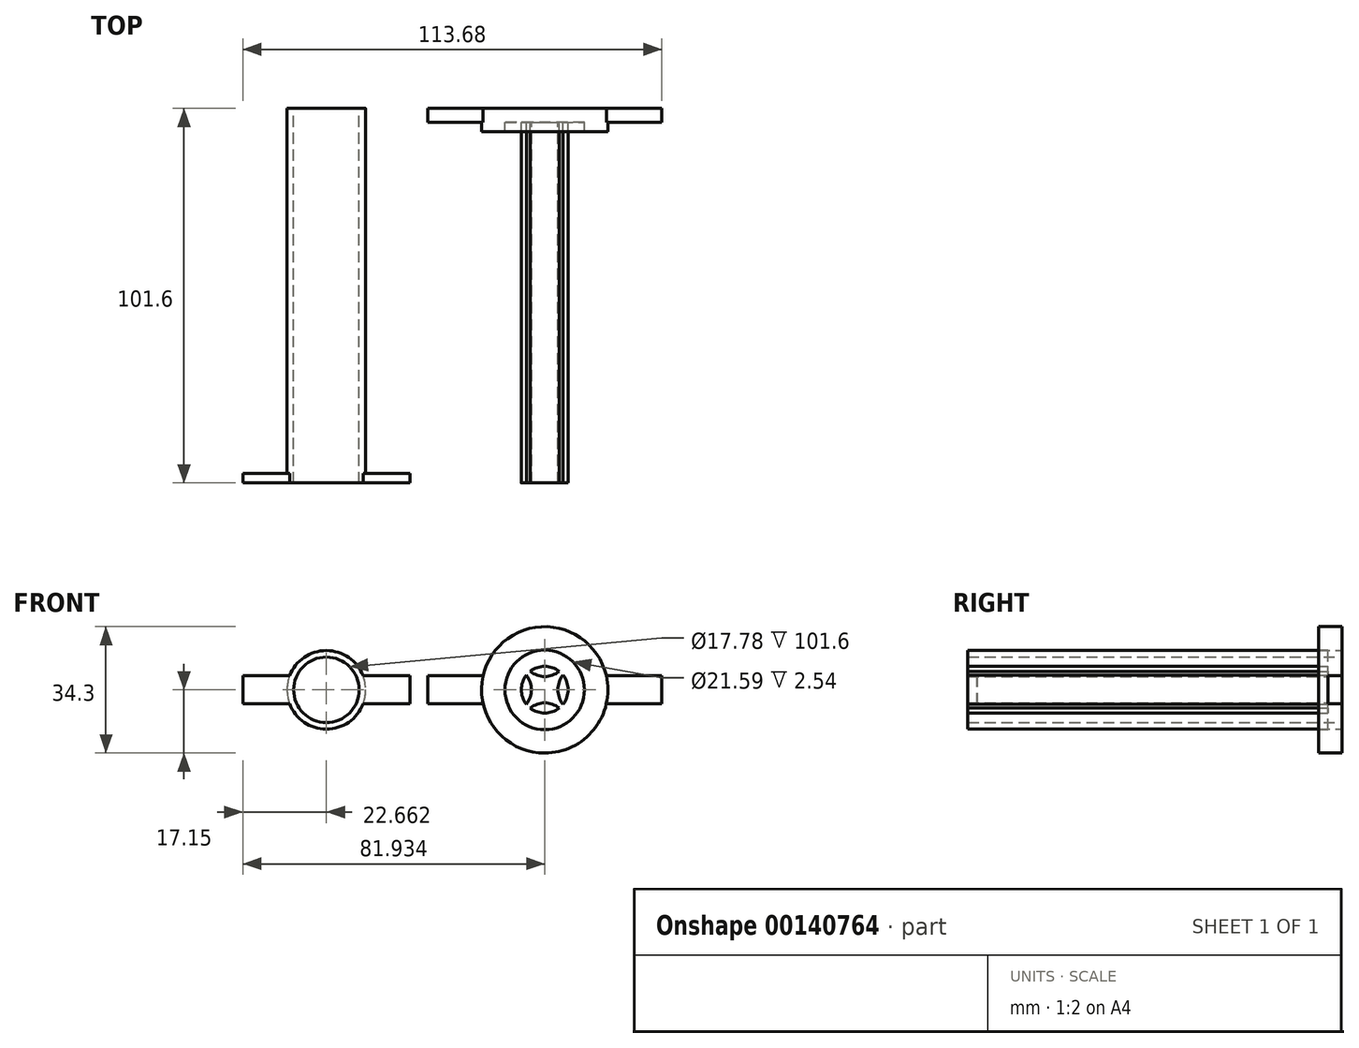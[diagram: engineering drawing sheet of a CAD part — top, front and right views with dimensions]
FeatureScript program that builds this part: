
annotation { "Feature Type Name" : "Feature", "Feature Type Description" : "" }
export const myFeature = defineFeature(function(context is Context, id is Id, definition is map)
    precondition{}
    {
        {
            var Q0;
            Q0=qCreatedBy(makeId("Front.planeOp"),FACE);
            var sketch = newSketch(context, id + "F0", { "sketchPlane" : qUnion([Q0])});
            skCircle(sketch, "E0", {"center": v(0, 0) * mm, "radius": 12.7 * mm});
            skCircle(sketch, "E1", {"center": v(0, 0) * mm, "radius": 15.24 * mm});
            skPoint(sketch, "E2.center", {"position": v(66.03, 0) * mm});
            skLineSegment(sketch, "E3", {"start": v(34.28, 0) * mm, "end": v(34.28, 3.8) * mm});
            skLineSegment(sketch, "E4", {"start": v(34.28, 3.8) * mm, "end": v(49.32, 3.8) * mm});
            skLineSegment(sketch, "E5", {"start": v(34.28, 0) * mm, "end": v(34.28, -3.81) * mm});
            skLineSegment(sketch, "E6", {"start": v(34.28, -3.81) * mm, "end": v(49.32, -3.81) * mm});
            skCircle(sketch, "E7", {"center": v(66.03, 0) * mm, "radius": 15.88 * mm});
            skCircle(sketch, "E8", {"center": v(66.03, 0) * mm, "radius": 17.15 * mm});
            skLineSegment(sketch, "E9.MirrorCS", {"start": v(97.78, -3.81) * mm, "end": v(82.75, -3.81) * mm});
            skLineSegment(sketch, "E10.MirrorCS", {"start": v(97.78, 0) * mm, "end": v(97.78, -3.81) * mm});
            skLineSegment(sketch, "E11.MirrorCS", {"start": v(97.78, 3.8) * mm, "end": v(82.75, 3.8) * mm});
            skLineSegment(sketch, "E12.MirrorCS", {"start": v(97.78, 0) * mm, "end": v(97.78, 3.8) * mm});
            skSolve(sketch);
        }
        {
            var Q0;
            Q0=makeQuery(id+"F0.imprint","IMPRINT",FACE,{"disambiguationData":[TD([[makeQuery(id+"F0.imprint","IMPRINT",EDGE,{"derivedFrom":sQuery(id+"F0.wireOp",EDGE,"WYK5WIV5-LSHk-n524-mOr9-z27NABO4Qitl")}),-1.0]])]});
            var Q1;
            Q1=makeQuery(id+"F0.imprint","IMPRINT",FACE,{"disambiguationData":[TD([[makeQuery(id+"F0.imprint","IMPRINT",EDGE,{"derivedFrom":sQuery(id+"F0.wireOp",EDGE,"E3")}),-1.0]])]});
            var Q2;
            {var subQ1=sQuery(id+"F0.wireOp",EDGE,"E9.MirrorCS");Q2=makeQuery(id+"F0.imprint","IMPRINT",FACE,{"disambiguationData":[TD([[makeQuery(id+"F0.imprint","IMPRINT",EDGE,{"derivedFrom":subQ1}),-1.0]])]});}
            var Q3;
            Q3=makeQuery(id+"F0.imprint","IMPRINT",FACE,{"disambiguationData":[TD([[makeQuery(id+"F0.imprint","IMPRINT",EDGE,{"derivedFrom":sQuery(id+"F0.wireOp",EDGE,"E7")}),-1.0]])]});
            var Q4;
            Q4=makeQuery(id+"F0.imprint","IMPRINT",FACE,{"disambiguationData":[TD([[makeQuery(id+"F0.imprint","IMPRINT",EDGE,{"derivedFrom":sQuery(id+"F0.wireOp",EDGE,"WYK5WIV5-LSHk-n524-mOr9-z27NABO4Qitl")}),1.0]])]});
            var Q5;
            Q5=makeQuery(id+"F0.imprint","IMPRINT",FACE,{"disambiguationData":[TD([[makeQuery(id+"F0.imprint","IMPRINT",EDGE,{"derivedFrom":sQuery(id+"F0.wireOp",EDGE,"E2.3.0")}),1.0]])]});
            var Q6;
            Q6=makeQuery(id+"F0.imprint","IMPRINT",FACE,{"disambiguationData":[TD([[makeQuery(id+"F0.imprint","IMPRINT",EDGE,{"derivedFrom":sQuery(id+"F0.wireOp",EDGE,"E2.2.0")}),1.0]])]});
            var Q7;
            Q7=makeQuery(id+"F0.imprint","IMPRINT",FACE,{"disambiguationData":[TD([[makeQuery(id+"F0.imprint","IMPRINT",EDGE,{"derivedFrom":sQuery(id+"F0.wireOp",EDGE,"E2.1.0")}),1.0]])]});
            var Q8;
            Q8=makeQuery(id+"F0.imprint","IMPRINT",FACE,{"disambiguationData":[TD([[makeQuery(id+"F0.imprint","IMPRINT",EDGE,{"derivedFrom":sQuery(id+"F0.wireOp",EDGE,"E7")}),1.0]])]});
            extrude(context, id + "F1", {"entities" : qUnion([Q0, Q1, Q2, Q3, Q4, Q5, Q6, Q7, Q8]), "depth" : 3.8 * mm});
        }
        {
            var Q0;
            Q0=makeQuery(id+"F1.opExtrude","CAP_FACE",FACE,{"disambiguationData":[OSD([sQuery(id+"F0.wireOp",EDGE,"WYK5WIV5-LSHk-n524-mOr9-z27NABO4Qitl"),sQuery(id+"F0.wireOp",EDGE,"E2.1.0"),sQuery(id+"F0.wireOp",EDGE,"E2.2.0"),sQuery(id+"F0.wireOp",EDGE,"E2.3.0"),sQuery(id+"F0.wireOp",EDGE,"E3"),sQuery(id+"F0.wireOp",EDGE,"E4"),sQuery(id+"F0.wireOp",EDGE,"E5"),sQuery(id+"F0.wireOp",EDGE,"E6"),sQuery(id+"F0.wireOp",EDGE,"E8"),sQuery(id+"F0.wireOp",EDGE,"E9.MirrorCS"),sQuery(id+"F0.wireOp",EDGE,"E10.MirrorCS"),sQuery(id+"F0.wireOp",EDGE,"E11.MirrorCS"),sQuery(id+"F0.wireOp",EDGE,"E12.MirrorCS")])],"isStart":false});
            var sketch = newSketch(context, id + "F2", { "sketchPlane" : qUnion([Q0])});
            skLineSegment(sketch, "E13.0.0", {"start": v(34.28, 3.8) * mm, "end": v(34.28, -3.81) * mm});
            skLineSegment(sketch, "E13.0.1", {"start": v(34.28, -3.81) * mm, "end": v(49.32, -3.81) * mm});
            skArc(sketch, "E13.0.2", {"start": v(49.32, -3.81) * mm, "mid": v(66.03, -17.15) * mm, "end": v(82.75, -3.8) * mm});
            skLineSegment(sketch, "E13.0.3", {"start": v(82.75, -3.81) * mm, "end": v(97.78, -3.81) * mm});
            skLineSegment(sketch, "E13.0.4", {"start": v(97.78, -3.81) * mm, "end": v(97.78, 3.8) * mm});
            skLineSegment(sketch, "E13.0.5", {"start": v(97.78, 3.8) * mm, "end": v(82.75, 3.8) * mm});
            skArc(sketch, "E13.0.6", {"start": v(82.75, 3.8) * mm, "mid": v(66.03, 17.15) * mm, "end": v(49.32, 3.8) * mm});
            skLineSegment(sketch, "E13.0.7", {"start": v(49.32, 3.8) * mm, "end": v(34.28, 3.8) * mm});
            skCircle(sketch, "E14", {"center": v(66.03, 0) * mm, "radius": 10.8 * mm});
            skCircle(sketch, "E15", {"center": v(66.03, 0) * mm, "radius": 17.15 * mm});
            skSolve(sketch);
        }
        {
            var Q0;
            Q0=makeQuery(id+"F2.imprint","IMPRINT",FACE,{"disambiguationData":[TD([[makeQuery(id+"F2.imprint","IMPRINT",EDGE,{"derivedFrom":sQuery(id+"F2.wireOp",EDGE,"E14")}),-1.0]])]});
            extrude(context, id + "F3", {"entities" : qUnion([Q0]), "operationType" : NewBodyOperationType.ADD, "depth" : 2.54 * mm});
        }
        {
            var Q0;
            Q0=qCreatedBy(makeId("Front.planeOp"),FACE);
            var sketch = newSketch(context, id + "F4", { "sketchPlane" : qUnion([Q0])});
            skCircle(sketch, "E16", {"center": v(6.76, 0) * mm, "radius": 10.67 * mm});
            skCircle(sketch, "E17", {"center": v(6.76, 0) * mm, "radius": 8.9 * mm});
            skSolve(sketch);
        }
        {
            var Q0;
            Q0=qSketchRegion(id+"F4",true);
            extrude(context, id + "F5", {"entities" : qUnion([Q0]), "depth" : 101.6 * mm});
        }
        {
            var Q0;
            Q0=qCreatedBy(makeId("Front.planeOp"),FACE);
            var sketch = newSketch(context, id + "F6", { "sketchPlane" : qUnion([Q0])});
            skCircle(sketch, "E18", {"center": v(66.03, 0.04) * mm, "radius": 6.35 * mm});
            skLineSegment(sketch, "E19.bottom", {"start": v(70.52, 4.53) * mm, "end": v(61.54, 4.53) * mm});
            skLineSegment(sketch, "E19.left", {"start": v(70.52, 4.53) * mm, "end": v(70.52, -4.45) * mm});
            skLineSegment(sketch, "E19.right", {"start": v(61.54, 4.53) * mm, "end": v(61.54, -4.45) * mm});
            skLineSegment(sketch, "E20", {"start": v(61.54, -4.45) * mm, "end": v(70.52, -4.45) * mm});
            skSolve(sketch);
        }
        {
            var Q0;
            Q0=makeQuery(id+"F5.opExtrude","CAP_FACE",FACE,{"disambiguationData":[OSD([sQuery(id+"F4.wireOp",EDGE,"E16"),sQuery(id+"F4.wireOp",EDGE,"E17")])],"isStart":false});
            var sketch = newSketch(context, id + "F7", { "sketchPlane" : qUnion([Q0])});
            skCircle(sketch, "E21.0", {"center": v(6.76, 0) * mm, "radius": 8.9 * mm});
            skLineSegment(sketch, "E22", {"start": v(6.76, 0) * mm, "end": v(6.76, 3.81) * mm});
            skLineSegment(sketch, "E23", {"start": v(-3.2, 3.81) * mm, "end": v(-15.9, 3.81) * mm});
            skLineSegment(sketch, "E24", {"start": v(-15.9, 3.81) * mm, "end": v(-15.9, -3.81) * mm});
            skPoint(sketch, "E25.start.orphan", {"position": v(6.76, -3.81) * mm});
            skLineSegment(sketch, "E26", {"start": v(-15.9, -3.81) * mm, "end": v(-3.2, -3.81) * mm});
            skLineSegment(sketch, "E27.MirrorCS", {"start": v(29.43, -3.81) * mm, "end": v(16.73, -3.81) * mm});
            skLineSegment(sketch, "E28.MirrorCS", {"start": v(29.43, 3.81) * mm, "end": v(29.43, -3.81) * mm});
            skLineSegment(sketch, "E29.MirrorCS", {"start": v(16.73, 3.81) * mm, "end": v(29.43, 3.81) * mm});
            skSolve(sketch);
        }
        {
            var Q0;
            {var subQ0=sQuery(id+"F7.wireOp",EDGE,"E23");Q0=makeQuery(id+"F7.imprint","IMPRINT",FACE,{"disambiguationData":[TD([[makeQuery(id+"F7.imprint","IMPRINT",EDGE,{"derivedFrom":subQ0}),1.0]])]});}
            var Q1;
            {var subQ0=sQuery(id+"F7.wireOp",EDGE,"E27.MirrorCS");Q1=makeQuery(id+"F7.imprint","IMPRINT",FACE,{"disambiguationData":[TD([[makeQuery(id+"F7.imprint","IMPRINT",EDGE,{"derivedFrom":subQ0}),-1.0]])]});}
            extrude(context, id + "F8", {"entities" : qUnion([Q0, Q1]), "operationType" : NewBodyOperationType.ADD, "oppositeDirection" : true, "depth" : 2.54 * mm});
        }
        {
            var Q0;
            Q0=makeQuery(id+"F3.boolean.opBoolean","SPLIT",FACE,{"disambiguationData":[TD([makeQuery(id+"F3.opExtrude","SWEPT_FACE",FACE,{"disambiguationData":[OSD([sQuery(id+"F2.wireOp",EDGE,"E14")])]})])],"derivedFrom":makeQuery(id+"F1.opExtrude","CAP_FACE",FACE,{"disambiguationData":[OSD([sQuery(id+"F0.wireOp",EDGE,"E3"),sQuery(id+"F0.wireOp",EDGE,"E4"),sQuery(id+"F0.wireOp",EDGE,"E5"),sQuery(id+"F0.wireOp",EDGE,"E6"),sQuery(id+"F0.wireOp",EDGE,"E8"),sQuery(id+"F0.wireOp",EDGE,"E9.MirrorCS"),sQuery(id+"F0.wireOp",EDGE,"E10.MirrorCS"),sQuery(id+"F0.wireOp",EDGE,"E11.MirrorCS"),sQuery(id+"F0.wireOp",EDGE,"E12.MirrorCS")])],"isStart":false})});
            var sketch = newSketch(context, id + "F9", { "sketchPlane" : qUnion([Q0])});
            skSolve(sketch);
        }
        {
            var Q0;
            Q0=makeQuery(id+"F9.imprint","IMPRINT",FACE,{"disambiguationData":[TD([[makeQuery(id+"F9.imprint","IMPRINT",EDGE,{"derivedFrom":makeQuery(id+"F3.opExtrude","CAP_EDGE",EDGE,{"disambiguationData":[OSD([sQuery(id+"F2.wireOp",EDGE,"E14")])],"isStart":true})}),1.0]])]});
            var sketch = newSketch(context, id + "F10", { "sketchPlane" : qUnion([Q0])});
            skPoint(sketch, "E30.middle", {"position": v(66.03, 0.04) * mm});
            skArc(sketch, "E31.0", {"start": v(61.06, 3.99) * mm, "mid": v(59.68, 0.04) * mm, "end": v(61.06, -3.91) * mm});
            skArc(sketch, "E32.trimOffspring", {"start": v(69.98, 5) * mm, "mid": v(66.03, 6.39) * mm, "end": v(62.08, 5) * mm});
            skArc(sketch, "E33.trimOffspring", {"start": v(62.08, -4.93) * mm, "mid": v(66.03, -6.31) * mm, "end": v(69.98, -4.93) * mm});
            skArc(sketch, "E34.trimOffspring", {"start": v(71, -3.91) * mm, "mid": v(72.38, 0.04) * mm, "end": v(71, 3.99) * mm});
            skArc(sketch, "E35.MirrorCS", {"start": v(61.06, 3.99) * mm, "mid": v(62.44, 0.04) * mm, "end": v(61.06, -3.91) * mm});
            skArc(sketch, "E36.MirrorCS", {"start": v(62.08, -4.93) * mm, "mid": v(66.03, -3.56) * mm, "end": v(69.98, -4.93) * mm});
            skArc(sketch, "E37.MirrorCS", {"start": v(71, -3.91) * mm, "mid": v(69.63, 0.04) * mm, "end": v(71, 3.99) * mm});
            skArc(sketch, "E38.MirrorCS", {"start": v(69.98, 5) * mm, "mid": v(66.03, 3.63) * mm, "end": v(62.08, 5) * mm});
            skSolve(sketch);
        }
        {
            var Q0;
            Q0 = qSketchRegion(id + "F10", true);
            extrude(context, id + "F11", {"entities" : qUnion([Q0]), "operationType" : NewBodyOperationType.ADD, "depth" : 97.8 * mm});
        }
    });
